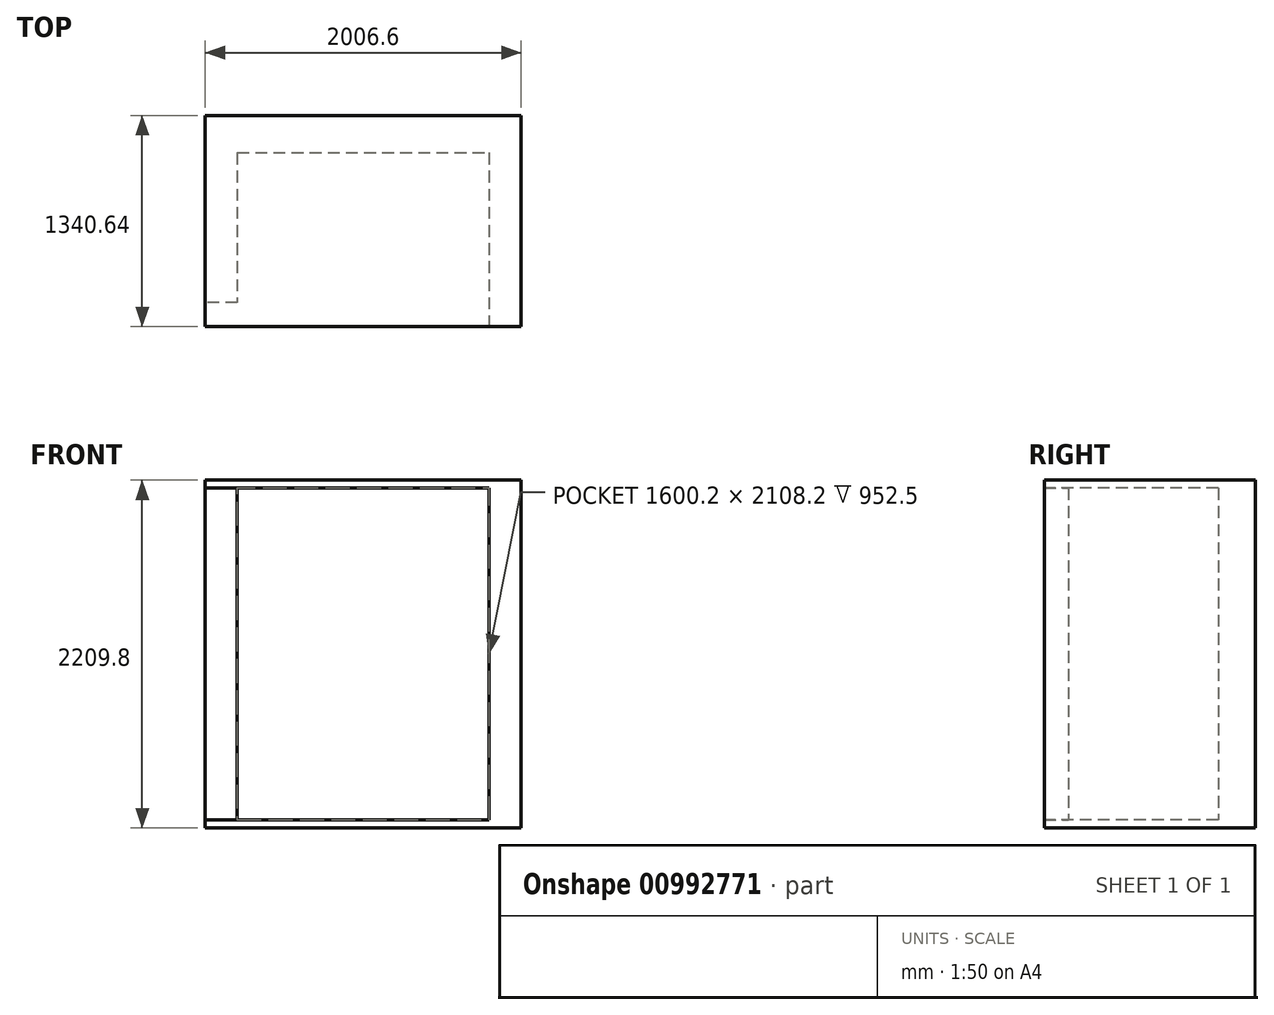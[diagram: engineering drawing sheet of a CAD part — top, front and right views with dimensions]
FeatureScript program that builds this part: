
annotation { "Feature Type Name" : "Feature", "Feature Type Description" : "" }
export const myFeature = defineFeature(function(context is Context, id is Id, definition is map)
    precondition{}
    {
        {
            var Q0;
            Q0=qCreatedBy(makeId("Top.planeOp"),FACE);
            var sketch = newSketch(context, id + "F0", { "sketchPlane" : qUnion([Q0])});
            skLineSegment(sketch, "E0", {"start": v(-800.1, 0) * mm, "end": v(800.1, 0) * mm});
            skLineSegment(sketch, "E1", {"start": v(-800.1, 0) * mm, "end": v(-800.1, -952.5) * mm});
            skLineSegment(sketch, "E2", {"start": v(800.1, 0) * mm, "end": v(800.1, -1104.9) * mm});
            skLineSegment(sketch, "E3", {"start": v(1003.3, -1104.9) * mm, "end": v(800.1, -1104.9) * mm});
            skLineSegment(sketch, "E4", {"start": v(-800.1, -952.5) * mm, "end": v(-1003.3, -952.5) * mm});
            skLineSegment(sketch, "E5", {"start": v(-1003.3, -952.5) * mm, "end": v(-1003.3, 235.74) * mm});
            skLineSegment(sketch, "E6", {"start": v(-1003.3, 235.74) * mm, "end": v(1003.3, 235.74) * mm});
            skLineSegment(sketch, "E7", {"start": v(1003.3, 235.74) * mm, "end": v(1003.3, -1104.9) * mm});
            skSolve(sketch);
        }
        {
            var Q0;
            Q0 = qSketchRegion(id + "F0", true);
            extrude(context, id + "F1", {"entities" : qUnion([Q0]), "depth" : 2108.2 * mm, "offsetDistance" : 25.4 * mm});
        }
        {
            var Q0;
            Q0=makeQuery(id+"F1.opExtrude","CAP_FACE",FACE,{"disambiguationData":[OSD([sQuery(id+"F0.wireOp",EDGE,"E0"),sQuery(id+"F0.wireOp",EDGE,"E1"),sQuery(id+"F0.wireOp",EDGE,"E2"),sQuery(id+"F0.wireOp",EDGE,"E3"),sQuery(id+"F0.wireOp",EDGE,"E4"),sQuery(id+"F0.wireOp",EDGE,"E5"),sQuery(id+"F0.wireOp",EDGE,"E6"),sQuery(id+"F0.wireOp",EDGE,"E7")])],"isStart":true});
            var sketch = newSketch(context, id + "F2", { "sketchPlane" : qUnion([Q0])});
            skLineSegment(sketch, "E8.bottom", {"start": v(-1003.3, -235.74) * mm, "end": v(1003.3, -235.74) * mm});
            skLineSegment(sketch, "E8.top", {"start": v(-1003.3, 1104.9) * mm, "end": v(1003.3, 1104.9) * mm});
            skLineSegment(sketch, "E8.left", {"start": v(-1003.3, -235.74) * mm, "end": v(-1003.3, 1104.9) * mm});
            skLineSegment(sketch, "E8.right", {"start": v(1003.3, -235.74) * mm, "end": v(1003.3, 1104.9) * mm});
            skSolve(sketch);
        }
        {
            var Q0;
            Q0 = qSketchRegion(id + "F2", true);
            extrude(context, id + "F3", {"entities" : qUnion([Q0]), "operationType" : NewBodyOperationType.ADD, "depth" : 50.8 * mm, "offsetDistance" : 25.4 * mm});
        }
        {
            var Q0;
            Q0=makeQuery(id+"F1.opExtrude","CAP_FACE",FACE,{"disambiguationData":[OSD([sQuery(id+"F0.wireOp",EDGE,"E0"),sQuery(id+"F0.wireOp",EDGE,"E1"),sQuery(id+"F0.wireOp",EDGE,"E2"),sQuery(id+"F0.wireOp",EDGE,"E3"),sQuery(id+"F0.wireOp",EDGE,"E4"),sQuery(id+"F0.wireOp",EDGE,"E5"),sQuery(id+"F0.wireOp",EDGE,"E6"),sQuery(id+"F0.wireOp",EDGE,"E7")])],"isStart":false});
            var sketch = newSketch(context, id + "F4", { "sketchPlane" : qUnion([Q0])});
            skLineSegment(sketch, "E9.bottom", {"start": v(1003.3, -1104.9) * mm, "end": v(-1003.3, -1104.9) * mm});
            skLineSegment(sketch, "E9.top", {"start": v(1003.3, 235.74) * mm, "end": v(-1003.3, 235.74) * mm});
            skLineSegment(sketch, "E9.left", {"start": v(1003.3, -1104.9) * mm, "end": v(1003.3, 235.74) * mm});
            skLineSegment(sketch, "E9.right", {"start": v(-1003.3, -1104.9) * mm, "end": v(-1003.3, 235.74) * mm});
            skSolve(sketch);
        }
        {
            var Q0;
            Q0 = qSketchRegion(id + "F4", true);
            extrude(context, id + "F5", {"entities" : qUnion([Q0]), "operationType" : NewBodyOperationType.ADD, "depth" : 50.8 * mm, "offsetDistance" : 25.4 * mm});
        }
    });
